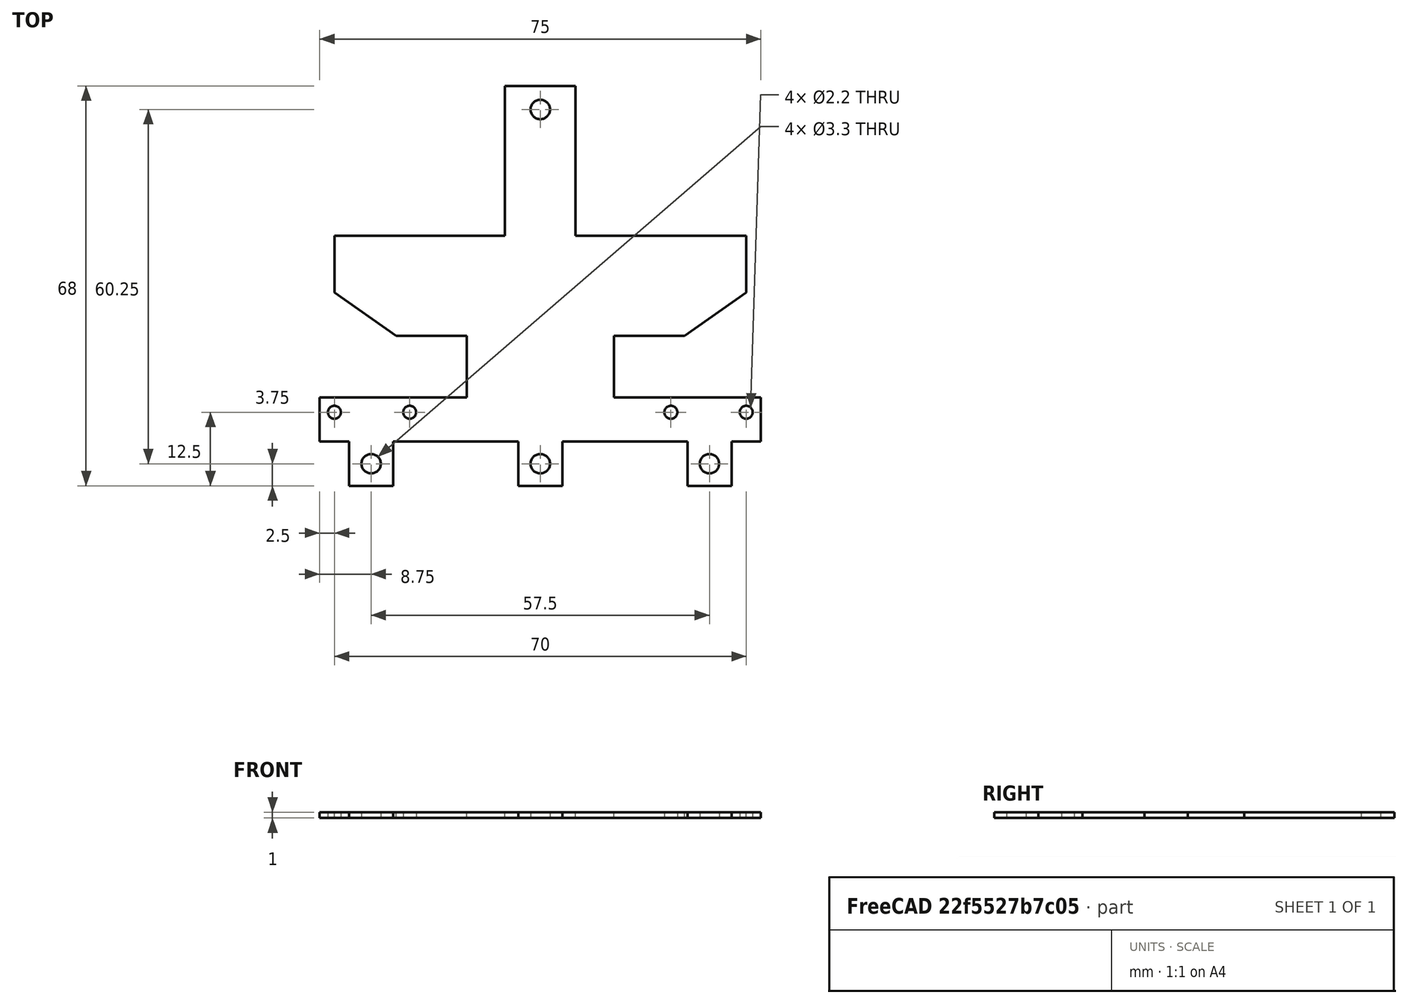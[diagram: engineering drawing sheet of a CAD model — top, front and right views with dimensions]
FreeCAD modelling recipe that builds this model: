
FCSTD DOCUMENT  (FreeCAD 0.17R13522 (Git))
Label: Distanzsensor_Halterung
License: All rights reserved
LicenseURL: http://en.wikipedia.org/wiki/All_rights_reserved
objects: Sketcher::SketchObject×3, PartDesign::Hole×2, Part::Extrusion×1, PartDesign::FeatureBase×1, PartDesign::Body×1, TechDraw::DrawSVGTemplate×1, TechDraw::DrawViewPart×1, TechDraw::DrawViewDimension×1, TechDraw::DrawPage×1
note: 10 computed .brp shape members not serialized (recipe doc carries the construction recipe); baked Part::Feature solids carry a one-line shape summary decoded from their .brp

FEATURE [Sketcher::SketchObject] Sketch
  sketch-geometry (30):
    g0: LineSegment StartX=0 StartY=0 StartZ=0 EndX=5 EndY=0 EndZ=0
    g1: LineSegment StartX=5 StartY=0 StartZ=0 EndX=5 EndY=-7.5 EndZ=0
    g2: LineSegment StartX=5 StartY=-7.5 StartZ=0 EndX=12.5 EndY=-7.5 EndZ=0
    g3: LineSegment StartX=12.5 StartY=-7.5 StartZ=0 EndX=12.5 EndY=0 EndZ=0
    g4: LineSegment StartX=12.5 StartY=0 StartZ=0 EndX=33.75 EndY=0 EndZ=0
    g5: LineSegment StartX=33.75 StartY=0 StartZ=0 EndX=33.75 EndY=-7.5 EndZ=0
    g6: LineSegment StartX=33.75 StartY=-7.5 StartZ=0 EndX=41.25 EndY=-7.5 EndZ=0
    g7: LineSegment StartX=41.25 StartY=-7.5 StartZ=0 EndX=41.25 EndY=0 EndZ=0
    g8: LineSegment StartX=41.25 StartY=0 StartZ=0 EndX=62.5 EndY=0 EndZ=0
    g9: LineSegment StartX=62.5 StartY=0 StartZ=0 EndX=62.5 EndY=-7.5 EndZ=0
    g10: LineSegment StartX=62.5 StartY=-7.5 StartZ=0 EndX=70 EndY=-7.5 EndZ=0
    g11: LineSegment StartX=70 StartY=-7.5 StartZ=0 EndX=70 EndY=0 EndZ=0
    g12: LineSegment StartX=70 StartY=0 StartZ=0 EndX=75 EndY=0 EndZ=0
    g13: LineSegment StartX=75 StartY=0 StartZ=0 EndX=75 EndY=7.5 EndZ=0
    g14: LineSegment StartX=75 StartY=7.5 StartZ=0 EndX=50 EndY=7.5 EndZ=0
    g15: LineSegment StartX=50 StartY=7.5 StartZ=0 EndX=50 EndY=18 EndZ=0
    g16: LineSegment StartX=50 StartY=18 StartZ=0 EndX=62 EndY=18 EndZ=0
    g17: LineSegment StartX=62 StartY=18 StartZ=0 EndX=72.5 EndY=25.3522 EndZ=0
    g18: LineSegment StartX=2.49999 StartY=25.3522 StartZ=0 EndX=13 EndY=18 EndZ=0
    g19: LineSegment StartX=13 StartY=18 StartZ=0 EndX=25 EndY=18 EndZ=0
    g20: LineSegment StartX=25 StartY=18 StartZ=0 EndX=25 EndY=7.5 EndZ=0
    g21: LineSegment StartX=25 StartY=7.5 StartZ=0 EndX=0 EndY=7.5 EndZ=0
    g22: LineSegment StartX=0 StartY=7.5 StartZ=0 EndX=0 EndY=0 EndZ=0
    g23: LineSegment StartX=2.49999 StartY=25.3522 StartZ=0 EndX=2.50001 EndY=35 EndZ=0
    g24: LineSegment StartX=2.50001 StartY=35 StartZ=0 EndX=31.5 EndY=35 EndZ=0
    g25: LineSegment StartX=31.5 StartY=35 StartZ=0 EndX=31.5 EndY=60.5 EndZ=0
    g26: LineSegment StartX=43.5 StartY=60.5 StartZ=0 EndX=43.5 EndY=35 EndZ=0
    g27: LineSegment StartX=43.5 StartY=35 StartZ=0 EndX=72.5 EndY=35 EndZ=0
    g28: LineSegment StartX=72.5 StartY=35 StartZ=0 EndX=72.5 EndY=25.3522 EndZ=0
    g29: LineSegment StartX=31.5 StartY=60.5 StartZ=0 EndX=43.5 EndY=60.5 EndZ=0
  constraints (89):
    c: Equal(g2,g6)
    c: Equal(g10,g6)
    c: Equal(g8,g4)
    c: Equal(g12,g0)
    c: Equal(g21,g14)
    c: Equal(g22,g13)
    c: Equal(g15,g20)
    c: Equal(g16,g19)
    c: Equal(g17,g18)
    c: Equal(g28,g23)
    c: Equal(g27,g24)
    c: Equal(g25,g26)
    c: Horizontal(g29)
    c: Coincident(g19,g20)
    c: Horizontal(g0)
    c: Horizontal(g4)
    c: Horizontal(g8)
    c: Horizontal(g12)
    c: Horizontal(g10)
    c: Horizontal(g6)
    c: Horizontal(g2)
    c: Horizontal(g14)
    c: Horizontal(g21)
    c: Horizontal(g16)
    c: Horizontal(g19)
    c: Horizontal(g27)
    c: Horizontal(g24)
    c: Vertical(g25)
    c: Vertical(g26)
    c: Coincident(g25,g29)
    c: Coincident(g29,g26)
    c: Coincident(g26,g27)
    c: Coincident(g24,g25)
    c: Coincident(g23,g24)
    c: Coincident(g23,g18)
    c: Coincident(g28,g27)
    c: Coincident(g17,g28)
    c: Coincident(g17,g16)
    c: Coincident(g16,g15)
    c: Vertical(g15)
    c: Vertical(g20)
    c: Coincident(g15,g14)
    c: Coincident(g14,g13)
    c: Coincident(g12,g13)
    c: Vertical(g22)
    c: Vertical(g13)
    c: Coincident(g12,g11)
    c: Vertical(g11)
    c: Vertical(g9)
    c: Vertical(g7)
    c: Vertical(g5)
    c: Vertical(g3)
    c: Vertical(g1)
    c: Coincident(g11,g10)
    c: Coincident(g10,g9)
    c: Coincident(g9,g8)
    c: Coincident(g8,g7)
    c: Coincident(g7,g6)
    c: Coincident(g6,g5)
    c: Coincident(g5,g4)
    c: Coincident(g4,g3)
    c: Coincident(g2,g3)
    c: Coincident(g2,g1)
    c: Coincident(g0,g1)
    c: Coincident(g0,g-1)
    c: Coincident(g22,g21)
    c: Coincident(g20,g21)
    c: Coincident(g19,g18)
    c: Coincident(g-1,g22)
    c: Horizontal(g18,g17)
    c: Horizontal(g20,g14)
    c: DistanceX(g6,g6) = 7.5
    c: DistanceX(g21,g20) = 25
    c: DistanceX(g23,g27) = 70
    c: Angle(g27,g28) = 1.5708
    c: DistanceX(g29,g29) = 12
    c: DistanceX(g-1,g12) = 75
    c: DistanceY(g13,g13) = 7.5
    c: DistanceY(g12,g15) = 18
    c: DistanceY(g26,g26) = 25.5
    c: DistanceY(g15,g27) = 17
    c: Angle(g18,g23) = 2.18166
    c: DistanceX(g18,g19) = 12
    c: DistanceY(g1,g1) = 7.5
    c: Equal(g1,g5)
    c: Equal(g9,g1)
    c: Horizontal(g3,g0)
    c: Horizontal(g7,g4)
    c: DistanceX(g-1,g0) = 5
FEATURE [Part::Extrusion] Extrude
  Base = -> Sketch
  Dir = (0,0,1)
  DirMode = 0
  FaceMakerClass = Part::FaceMakerBullseye
  LengthFwd = 1
  LengthRev = 0
  Solid = true
  Symmetric = false
FEATURE [Sketcher::SketchObject] Sketch001
  MapMode = 5
  Placement = pos=(0,0,1) rot=(0,0,1;0rad)
  Support = -> [Extrude]
  sketch-geometry (4):
    g0: Circle CenterX=2.5 CenterY=5 CenterZ=0 NormalX=0 NormalY=0 NormalZ=1 AngleXU=0 Radius=1.1
    g1: Circle CenterX=15.3 CenterY=5 CenterZ=0 NormalX=0 NormalY=0 NormalZ=1 AngleXU=0 Radius=1.1
    g2: Circle CenterX=59.7 CenterY=5 CenterZ=0 NormalX=0 NormalY=0 NormalZ=1 AngleXU=0 Radius=1.1
    g3: Circle CenterX=72.5 CenterY=5 CenterZ=0 NormalX=0 NormalY=0 NormalZ=1 AngleXU=0 Radius=1.1
  constraints (12):
    c: Radius(g0) = 1.1
    c: Radius(g1) = 1.1
    c: Radius(g2) = 1.1
    c: Radius(g3) = 1.1
    c: Horizontal(g0,g1)
    c: Horizontal(g2,g0)
    c: Horizontal(g3,g0)
    c: DistanceX(g0,g1) = 12.8
    c: DistanceX(g2,g3) = 12.8
    c: DistanceX(g-1,g0) = 2.5
    c: DistanceY(g-1,g0) = 5
    c: DistanceX(g-1,g3) = 72.5
FEATURE [PartDesign::FeatureBase] BaseFeature
  BaseFeature = -> Extrude
FEATURE [PartDesign::Hole] Hole
  BaseFeature = -> BaseFeature
  Depth = 5
  DepthType = 0
  Diameter = 2.2
  DrillPoint = 1
  DrillPointAngle = 118
  HoleCutCountersinkAngle = 90
  HoleCutDepth = 0
  HoleCutDiameter = 2
  HoleCutType = 0
  ModelActualThread = false
  Profile = -> Sketch001
  Tapered = false
  TaperedAngle = 90
  ThreadAngle = 0
  ThreadClass = 0
  ThreadCutOffInner = 0
  ThreadCutOffOuter = 0
  ThreadDirection = 0
  ThreadFit = 0
  ThreadPitch = 0
  ThreadSize = 1
  ThreadType = 1
  Threaded = false
FEATURE [Sketcher::SketchObject] Sketch002
  MapMode = 5
  Placement = pos=(0,0,1) rot=(0,0,1;0rad)
  Support = -> [Hole]
  sketch-geometry (4):
    g0: Circle CenterX=8.75 CenterY=-3.75 CenterZ=0 NormalX=0 NormalY=0 NormalZ=1 AngleXU=0 Radius=1.65
    g1: Circle CenterX=37.5 CenterY=-3.75 CenterZ=0 NormalX=0 NormalY=0 NormalZ=1 AngleXU=0 Radius=1.65
    g2: Circle CenterX=66.25 CenterY=-3.75 CenterZ=0 NormalX=0 NormalY=0 NormalZ=1 AngleXU=0 Radius=1.65
    g3: Circle CenterX=37.5 CenterY=56.5 CenterZ=0 NormalX=0 NormalY=0 NormalZ=1 AngleXU=0 Radius=1.65
  constraints (12):
    c: Radius(g0) = 1.65
    c: Radius(g1) = 1.65
    c: Radius(g2) = 1.65
    c: Horizontal(g0,g1)
    c: Horizontal(g2,g0)
    c: Radius(g3) = 1.65
    c: Vertical(g3,g1)
    c: DistanceX(g-1,g1) = 37.5
    c: DistanceY(g1,g-1) = 3.75
    c: DistanceX(g-1,g0) = 8.75
    c: DistanceX(g-1,g2) = 66.25
    c: DistanceY(g-1,g3) = 56.5
FEATURE [PartDesign::Hole] Hole001
  BaseFeature = -> Hole
  Depth = 3
  DepthType = 0
  Diameter = 3.3
  DrillPoint = 1
  DrillPointAngle = 118
  HoleCutCountersinkAngle = 90
  HoleCutDepth = 0
  HoleCutDiameter = 3
  HoleCutType = 0
  ModelActualThread = false
  Profile = -> Sketch002
  Tapered = false
  TaperedAngle = 90
  ThreadAngle = 0
  ThreadClass = 0
  ThreadCutOffInner = 0
  ThreadCutOffOuter = 0
  ThreadDirection = 0
  ThreadFit = 0
  ThreadPitch = 0
  ThreadSize = 3
  ThreadType = 1
  Threaded = false
FEATURE [PartDesign::Body] Body
  BaseFeature = -> Extrude
  Group = -> [BaseFeature,Sketch001,Hole,Sketch002,Hole001]
  Origin = -> Origin
  Tip = -> Hole001
FEATURE [TechDraw::DrawSVGTemplate] Template
  EditableTexts = Designed_by_Name=Designed by Name; Drawing_number=Drawing number; FC-Date=Date; FC-SC=Scale; FC-SH=Sheet; FC-Title=Title; Subtitle=Subtitle; Weight=Weight
  Height = 210
  Orientation = 1
  Width = 297
FEATURE [TechDraw::DrawViewPart] View
  CoarseView = false
  Direction = (0,0,1)
  Focus = 100
  HardHidden = false
  IsoCount = 0
  IsoHidden = false
  IsoVisible = false
  LockPosition = false
  Perspective = false
  Rotation = 0
  ScaleType = 0
  SeamHidden = false
  SeamVisible = false
  SmoothHidden = false
  SmoothVisible = false
  Source = -> [Hole001]
  X = 73.7104
  Y = 128.786
FEATURE [TechDraw::DrawViewDimension] Dimension
  FormatSpec = %.2f
  LockPosition = false
  MeasureType = 1
  References2D = -> [View]
  Rotation = 0
  ScaleType = 0
  Type = 2
  X = 40.978
  Y = 51.6513
FEATURE [TechDraw::DrawPage] Page
  KeepUpdated = true
  ProjectionType = 0
  Template = -> Template
  Views = -> [View,Dimension]
